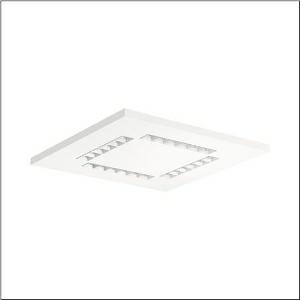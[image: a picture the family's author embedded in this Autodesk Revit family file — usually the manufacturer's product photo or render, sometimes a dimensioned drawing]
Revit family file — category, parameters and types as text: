
# Revit family: silica_r__21_square_51mx6ndu44w_bc45
name_source: partatom
category: Lighting Fixtures
units: mm (PartAtom-declared; Revit-internal decimal feet)

## family parameters
Cut with Voids When Loaded = No
Host = Face
Light Source = No
Part Type = Normal
Room Calculation Point = No
Round Connector Dimension = Use Diameter
Shared = No

## types (1)
- --- (1 x LED, 4600 lm, 27 W, 4000K)
    Apparent Load = 27 VA
    CIE Flux Codes = 83 98 100 100 100
    Color Rendering = 80
    Color Temperature = 4000K
    Default Elevation = 1800 mm
    Description = Silica® 21 Square, office luminaire, primary light control with lens, of PMMA, primary anti-glare with reflector, of PC, white, CAT 2 (L<= 3000cd/m²), light emission: direct distribution, primary light characteristic: symmetric, installation type: lay-in mounting, LED, rated luminous flux: 4.600lm, luminous efficacy: 170lm/W, light colour: 840, colour temperature: 4000K, control gear: DALI 2, with terminal, 5-pole, mains connection: 220..240V, AC, 50/60Hz, rated input power: 27W, luminaire housing, of aluminium, traffic white (RAL 9016), module: M625, length: 622mm, width: 622mm, height: 32mm, protection rating (complete): IP20, insulation class (complete): insulation class I (protective earthing), certification: CE, ENEC, VDE, permissible operating ambient temperature: 0..+35°C, standard: EN 50419, packaging unit: 1 piece
    Height = 0 mm  [stored 0 ft]
    Lamp = 1 x LED
    Lamp Light Flux = 4600 lm
    Lamp Power = 27 W
    Lamp count = 1
    Length = 622 mm
    Luminous efficacy = 170 lm/W
    Manufacturer = Siteco
    ModVariant = No
    Model = 51MX6NDU44W
    Mounting Place = Ceiling
    Mounting Type = Recessed
    Number of Poles = 1
    OnlyDefault = Yes
    Power Factor = 1
    Product Name = Silica® 21 Square
    Product group = office luminaire | ceiling recessed
    ProductGroupID = 401
    Protection Class = Protection class I
    Protection Degree = IP 20
    RLX_Detail_Level = 1
    RLX_Emergency_Light_Flux = 0 lm
    RLX_Emergency_Type = 0
    RLX_Emergency_Type_DB = No
    RlxData = <blob elided: 19025 chars, md5=d2476783>
    Socket = socket
    Standby Power = 0 W
    System Light Flux = 4600 lm
    System Power = 27 W
    Type Comments = factory setting: luminous flux: 100 % | dim-lin: 254 | 366 mA
    Type Image = l_1275224.jpg
    URL = http://relux.com
    VarID = @adj_083362
    Voltage = 0 V
    Weight = 0.00 kg
    Width = 622 mm

note: [stored X ft] marks values corroborated as IEEE doubles in the binary element streams (Revit-internal decimal feet)

## geometry (parser evidence)
native form markers: Blend x4, Sweep x9
no freeform markers — native parametric forms only
